# Revit family: Namika_Toilet Roll Holder_RFA
name_source: partatom
category: Generic Models
units: mm (PartAtom-declared; Revit-internal decimal feet)

## family parameters
Always vertical = Yes
Can host rebar = No
Cut with Voids When Loaded = No
Maintain Annotation Orientation = No
OmniClass Number = 23.21.43.15.31
Part Type = Normal
Room Calculation Point = No
Round Connector Dimension = Use Diameter
Shared = No
Work Plane-Based = No

## types (1)
- Standard
    Default Elevation = 0 mm  [stored 0 ft]
    Description = Namika Toilet Roll Holder
    Keywords = Toilet Roll Holder, Reeded
    Manufacturer = Abi Interiors Pty Ltd
    Part Number = Brushed Brass (15679), Brushed Copper (15680), Brushed Gunmetal (15681), Brushed Nickel (15682)
    Project = Namika Collection
    QR Link = abi.guide/CAJKCb
    Spec Image = https://cdn.bfldr.com
    Title = Namika Toilet Roll Holder

note: [stored X ft] marks values corroborated as IEEE doubles in the binary element streams (Revit-internal decimal feet)

## geometry (parser evidence)
native form markers: Sweep x3
no freeform markers — native parametric forms only
